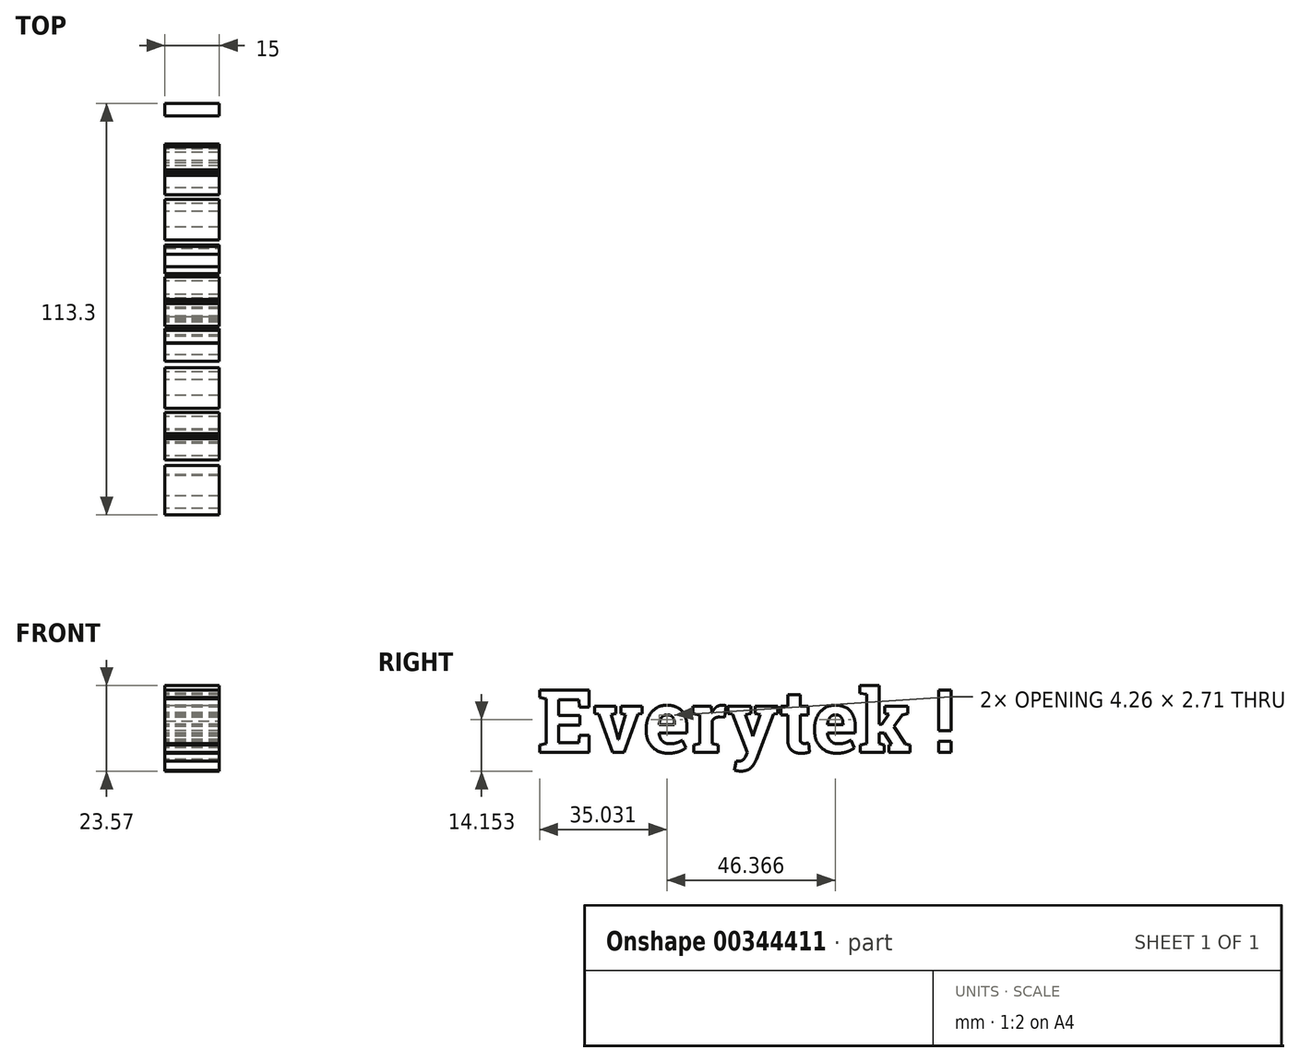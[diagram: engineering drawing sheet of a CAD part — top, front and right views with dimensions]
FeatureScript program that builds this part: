
annotation { "Feature Type Name" : "Feature", "Feature Type Description" : "" }
export const myFeature = defineFeature(function(context is Context, id is Id, definition is map)
    precondition{}
    {
        {
            var Q0;
            Q0=qCreatedBy(makeId("Right.planeOp"),FACE);
            var sketch = newSketch(context, id + "F0", { "sketchPlane" : qUnion([Q0])});
            skText(sketch, "E0", { "text": "Everytek !\n", "fontName": "RobotoSlab-Bold.ttf"});
            const initialGuessF0  = {"E0": [-0.06192, 0.0035, 1, 0, 0.0174]};
            skSetInitialGuess(sketch, initialGuessF0);
            skSolve(sketch);
        }
        {
            var Q0;
            Q0 = qSketchRegion(id + "F0", true);
            extrude(context, id + "F1", {"entities" : qUnion([Q0]), "depth" : 15 * mm});
        }
    });
